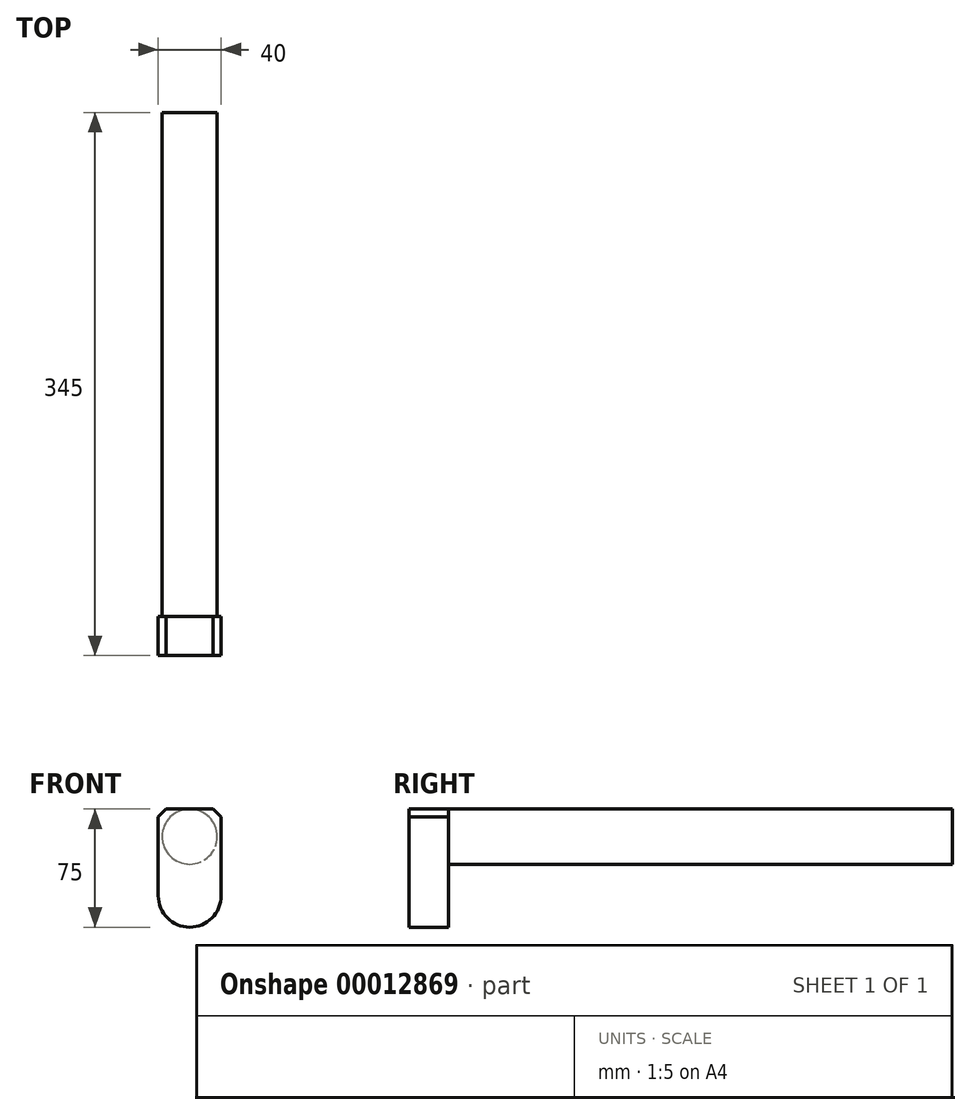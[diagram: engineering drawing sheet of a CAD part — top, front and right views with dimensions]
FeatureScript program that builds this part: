
annotation { "Feature Type Name" : "Feature", "Feature Type Description" : "" }
export const myFeature = defineFeature(function(context is Context, id is Id, definition is map)
    precondition{}
    {
        {
            var Q0;
            Q0=qCreatedBy(makeId("Front.planeOp"),FACE);
            var sketch = newSketch(context, id + "F0", { "sketchPlane" : qUnion([Q0])});
            skLineSegment(sketch, "E0.bottom", {"start": v(-20, 55) * mm, "end": v(20, 55) * mm});
            skLineSegment(sketch, "E0.top", {"start": v(-20, -20) * mm, "end": v(20, -20) * mm});
            skLineSegment(sketch, "E0.left", {"start": v(-20, 55) * mm, "end": v(-20, -20) * mm});
            skLineSegment(sketch, "E0.right", {"start": v(20, 55) * mm, "end": v(20, -20) * mm});
            skCircle(sketch, "E1", {"center": v(0, -20) * mm, "radius": 20 * mm, "construction": true});
            skLineSegment(sketch, "E2", {"start": v(0, -20) * mm, "end": v(0, 0) * mm});
            skCircle(sketch, "E3", {"center": v(0, 0) * mm, "radius": 20 * mm});
            skSolve(sketch);
        }
        {
            var Q0;
            {var subQ0=sQuery(id+"F0.wireOp",EDGE,"E0.bottom");Q0=makeQuery(id+"F0.imprint","IMPRINT",FACE,{"disambiguationData":[TD([[makeQuery(id+"F0.imprint","IMPRINT",EDGE,{"derivedFrom":subQ0}),-1.0]])]});}
            var Q1;
            {var subQ0=sQuery(id+"F0.wireOp",EDGE,"E3");var subQ1=makeQuery(id+"F0.imprint","INTERSECT",VERTEX,{"derivedFrom":[sQuery(id+"F0.wireOp",EDGE,"E0.left"),subQ0]});Q1=makeQuery(id+"F0.imprint","IMPRINT",FACE,{"disambiguationData":[TD([[makeQuery(id+"F0.imprint","IMPRINT",EDGE,{"disambiguationData":[TD([[subQ1,1.0]])],"derivedFrom":subQ0}),1.0]])]});}
            extrude(context, id + "F1", {"entities" : qUnion([Q0, Q1]), "depth" : 25 * mm});
        }
        {
            var Q0;
            {var subQ0=sQuery(id+"F0.wireOp",EDGE,"E0.bottom");Q0=makeQuery(id+"F0.imprint","IMPRINT",FACE,{"disambiguationData":[TD([[makeQuery(id+"F0.imprint","IMPRINT",EDGE,{"derivedFrom":subQ0}),-1.0]])]});}
            var sketch = newSketch(context, id + "F2", { "sketchPlane" : qUnion([Q0])});
            skCircle(sketch, "E4", {"center": v(0, 37.5) * mm, "radius": 17.5 * mm});
            skLineSegment(sketch, "E5", {"start": v(0, -20.52) * mm, "end": v(0, 37.5) * mm, "construction": true});
            skSolve(sketch);
        }
        {
            var Q0;
            Q0 = qSketchRegion(id + "F2", true);
            extrude(context, id + "F3", {"entities" : qUnion([Q0]), "operationType" : NewBodyOperationType.ADD, "oppositeDirection" : true, "depth" : 320 * mm});
        }
        {
            var Q0;
            Q0=makeQuery(id+"F1.opExtrude","SWEPT_EDGE",EDGE,{"disambiguationData":[OSD([sQuery(id+"F0.wireOp",EDGE,"E0.bottom"),sQuery(id+"F0.wireOp",EDGE,"E0.right")])]});
            var Q1;
            Q1=makeQuery(id+"F1.opExtrude","SWEPT_EDGE",EDGE,{"disambiguationData":[OSD([sQuery(id+"F0.wireOp",EDGE,"E0.bottom"),sQuery(id+"F0.wireOp",EDGE,"E0.left")])]});
            chamfer(context, id + "F4", {"entities" : qUnion([Q0, Q1]), "width" : 5 * mm, "tangentPropagation" : true});
        }
    });
